# Revit family: Urimat - Ecoplus
name_source: partatom
category: Plumbing Fixtures
revit_build: Autodesk Revit 2018 (Build: 20181015_0930(x64)
units: mm (PartAtom-declared; Revit-internal decimal feet)

## family parameters
Always vertical = Yes
Cut with Voids When Loaded = No
OmniClass Number = 23.45.05.21.11.21
OmniClass Title = Urinals
Part Type = Normal
Room Calculation Point = No
Round Connector Dimension = Use Diameter
Shared = No
Work Plane-Based = No

## types (1)
- Urimat - Ecoplus
    CW Connection = Yes
    Code = 16001
    Cold water connection Diameter = 15 mm
    Cold water connection Flowrate = 0.0 L/s
    Color = white
    Depth = 390 mm  [stored 1.27953 ft]
    HW Connection = No
    Height = 800 mm  [stored 2.62467 ft]
    Manufacturer = Urimat
    Material = <By Category>
    Material 2 = <By Category>
    Material type = polycarbonate
    Product line subcategory = Eco
    R1 = 410 mm
    R2 = 800 mm  [stored 2.62467 ft]
    R3 = 390 mm  [stored 1.27953 ft]
    R4 = 15 mm  [stored 0.0492126 ft]
    R5 = 50 mm  [stored 0.164042 ft]
    Vent Connection = No
    W1 = No
    Waste Connection = Yes
    Waste Connection Flowrate = 0.0 L/s
    Waste connection Diameter = 50 mm
    Weight = 4.40 kg
    Width = 410 mm
    With display = No

note: [stored X ft] marks values corroborated as IEEE doubles in the binary element streams (Revit-internal decimal feet)

## geometry (parser evidence)
native form markers: Blend x2, Sweep x3
no freeform markers — native parametric forms only
